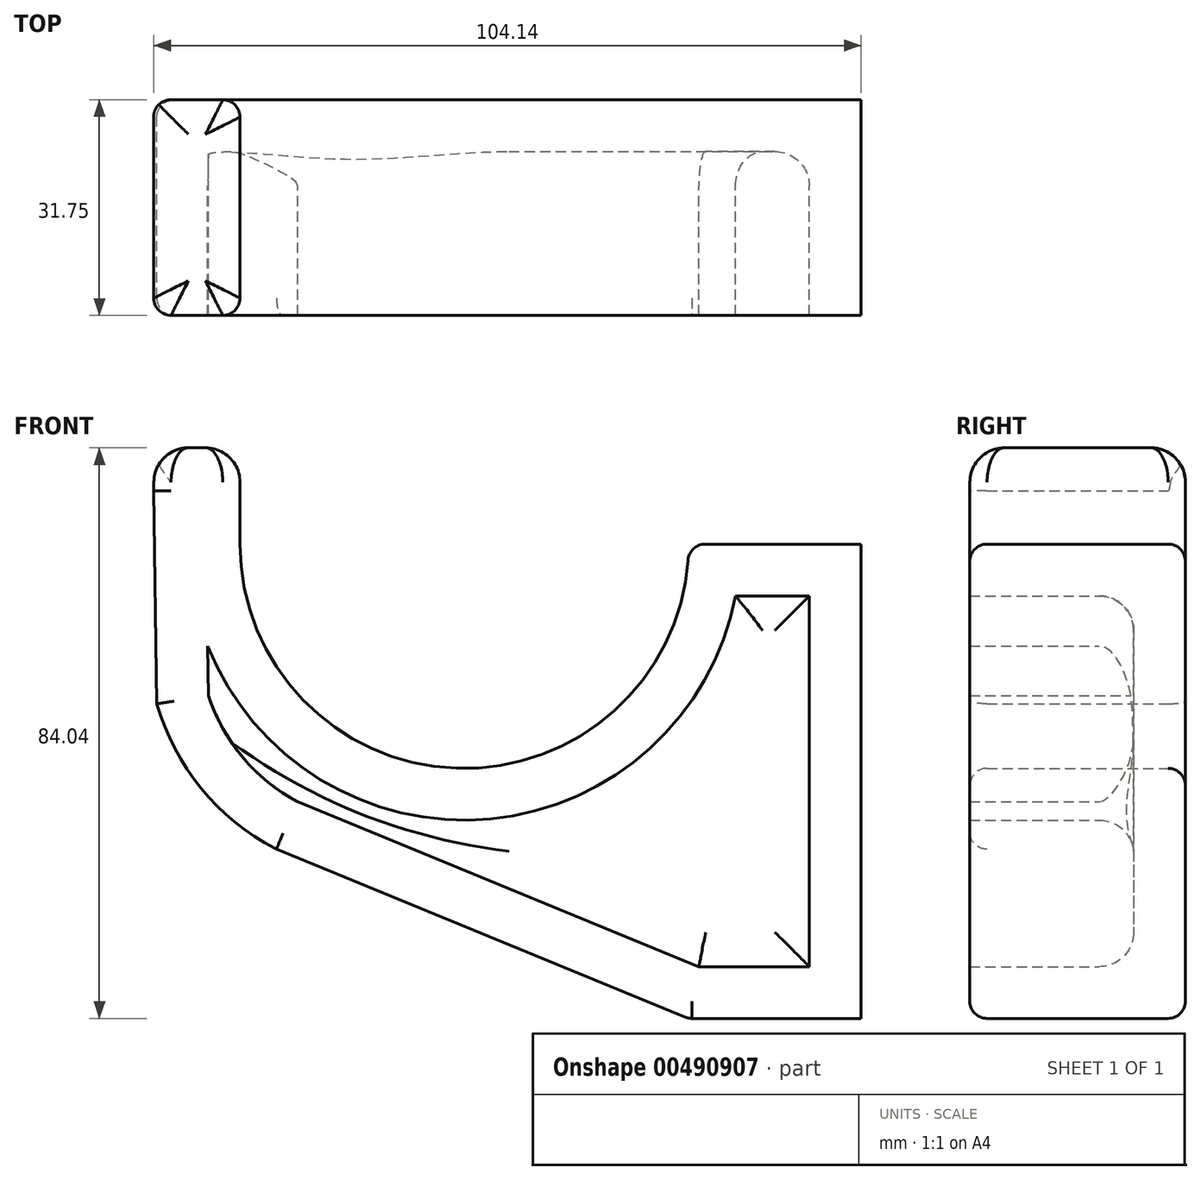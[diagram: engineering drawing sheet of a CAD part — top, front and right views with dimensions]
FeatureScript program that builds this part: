
annotation { "Feature Type Name" : "Feature", "Feature Type Description" : "" }
export const myFeature = defineFeature(function(context is Context, id is Id, definition is map)
    precondition{}
    {
        {
            var Q0;
            Q0=qCreatedBy(makeId("Front.planeOp"),FACE);
            var sketch = newSketch(context, id + "F0", { "sketchPlane" : qUnion([Q0])});
            skLineSegment(sketch, "E0", {"start": v(19.3, 23.5) * mm, "end": v(19.3, -46.34) * mm});
            skLineSegment(sketch, "E1", {"start": v(19.3, -46.34) * mm, "end": v(-6.1, -46.34) * mm});
            skLineSegment(sketch, "E2", {"start": v(-84.39, 0) * mm, "end": v(-84.84, 31.35) * mm});
            skArc(sketch, "E3", {"start": v(-72.14, 23.5) * mm, "mid": v(-39.12, -9.51) * mm, "end": v(-6.1, 23.5) * mm});
            skLineSegment(sketch, "E4", {"start": v(-6.1, 23.5) * mm, "end": v(19.3, 23.5) * mm});
            skLineSegment(sketch, "E5.top", {"start": v(-72.14, 37.7) * mm, "end": v(-84.84, 37.7) * mm});
            skLineSegment(sketch, "E5.left", {"start": v(-72.14, 23.5) * mm, "end": v(-72.14, 37.7) * mm});
            skLineSegment(sketch, "E5.right", {"start": v(-84.84, 17.4) * mm, "end": v(-84.84, 37.7) * mm});
            skArc(sketch, "E6", {"start": v(-84.39, 0) * mm, "mid": v(-77.83, -12.48) * mm, "end": v(-66.89, -21.36) * mm});
            skLineSegment(sketch, "E7", {"start": v(-66.89, -21.36) * mm, "end": v(-6.1, -46.34) * mm});
            skSolve(sketch);
        }
        {
            var Q0;
            Q0 = qSketchRegion(id + "F0", true);
            extrude(context, id + "F1", {"entities" : qUnion([Q0]), "depth" : 31.75 * mm});
        }
        {
            var Q0;
            Q0=makeQuery(id+"F1.opExtrude","CAP_FACE",FACE,{"disambiguationData":[OSD([sQuery(id+"F0.wireOp",EDGE,"E0"),sQuery(id+"F0.wireOp",EDGE,"E1"),sQuery(id+"F0.wireOp",EDGE,"E2"),sQuery(id+"F0.wireOp",EDGE,"E3"),sQuery(id+"F0.wireOp",EDGE,"E4"),sQuery(id+"F0.wireOp",EDGE,"E5.top"),sQuery(id+"F0.wireOp",EDGE,"E5.left"),sQuery(id+"F0.wireOp",EDGE,"E5.right"),sQuery(id+"F0.wireOp",EDGE,"E6"),sQuery(id+"F0.wireOp",EDGE,"E7")])],"isStart":false});
            shell(context, id + "F2", {"entities" : qUnion([Q0]), "thickness" : 7.62 * mm});
        }
        {
            var Q0;
            Q0=makeQuery(id+"F2.opShell","OFFSET_FACE",FACE,{"disambiguationData":[OSD([sQuery(id+"F0.wireOp",EDGE,"E0"),sQuery(id+"F0.wireOp",EDGE,"E1"),sQuery(id+"F0.wireOp",EDGE,"E2"),sQuery(id+"F0.wireOp",EDGE,"E3"),sQuery(id+"F0.wireOp",EDGE,"E4"),sQuery(id+"F0.wireOp",EDGE,"E5.top"),sQuery(id+"F0.wireOp",EDGE,"E5.left"),sQuery(id+"F0.wireOp",EDGE,"E5.right"),sQuery(id+"F0.wireOp",EDGE,"E6"),sQuery(id+"F0.wireOp",EDGE,"E7")])]});
            fillet(context, id + "F3", {"entities" : qUnion([Q0]), "radius" : 5.08 * mm, "tangentPropagation" : true, "allowEdgeOverflow" : false});
        }
        {
            var Q0;
            Q0=makeQuery(id+"F1.opExtrude","SWEPT_FACE",FACE,{"disambiguationData":[OSD([sQuery(id+"F0.wireOp",EDGE,"E5.top")])]});
            fillet(context, id + "F4", {"entities" : qUnion([Q0]), "radius" : 5.08 * mm, "tangentPropagation" : true, "allowEdgeOverflow" : false});
        }
        {
            var Q0;
            Q0=makeQuery(id+"F1.opExtrude","CAP_EDGE",EDGE,{"disambiguationData":[OSD([sQuery(id+"F0.wireOp",EDGE,"E4")])],"isStart":false});
            fillet(context, id + "F5", {"entities" : qUnion([Q0]), "radius" : 2.54 * mm, "tangentPropagation" : true, "allowEdgeOverflow" : false});
        }
        {
            var Q0;
            Q0=makeQuery(id+"F1.opExtrude","CAP_EDGE",EDGE,{"disambiguationData":[OSD([sQuery(id+"F0.wireOp",EDGE,"E4")])],"isStart":true});
            fillet(context, id + "F6", {"entities" : qUnion([Q0]), "radius" : 2.54 * mm, "tangentPropagation" : true, "allowEdgeOverflow" : false});
        }
        {
            var Q0;
            Q0=makeQuery(id+"F1.opExtrude","CAP_EDGE",EDGE,{"disambiguationData":[OSD([sQuery(id+"F0.wireOp",EDGE,"E1")])],"isStart":false});
            fillet(context, id + "F7", {"entities" : qUnion([Q0]), "radius" : 2.54 * mm, "tangentPropagation" : true, "allowEdgeOverflow" : false});
        }
        {
            var Q0;
            Q0=makeQuery(id+"F1.opExtrude","CAP_EDGE",EDGE,{"disambiguationData":[OSD([sQuery(id+"F0.wireOp",EDGE,"E7")])],"isStart":false});
            fillet(context, id + "F8", {"entities" : qUnion([Q0]), "radius" : 2.54 * mm, "tangentPropagation" : true, "allowEdgeOverflow" : false});
        }
        {
            var Q0;
            Q0=makeQuery(id+"F1.opExtrude","SWEPT_EDGE",EDGE,{"disambiguationData":[OSD([sQuery(id+"F0.wireOp",EDGE,"E3"),sQuery(id+"F0.wireOp",EDGE,"E4")])]});
            var Q1;
            Q1=makeQuery(id+"F1.opExtrude","CAP_EDGE",EDGE,{"disambiguationData":[OSD([sQuery(id+"F0.wireOp",EDGE,"E5.right")])],"isStart":false});
            var Q2;
            Q2=makeQuery(id+"F1.opExtrude","CAP_EDGE",EDGE,{"disambiguationData":[OSD([sQuery(id+"F0.wireOp",EDGE,"E2")])],"isStart":false});
            var Q3;
            Q3=makeQuery(id+"F1.opExtrude","CAP_EDGE",EDGE,{"disambiguationData":[OSD([sQuery(id+"F0.wireOp",EDGE,"E6")])],"isStart":false});
            fillet(context, id + "F9", {"entities" : qUnion([Q0, Q1, Q2, Q3]), "radius" : 2.54 * mm, "tangentPropagation" : true, "allowEdgeOverflow" : false});
        }
        {
            var Q0;
            Q0=makeQuery(id+"F1.opExtrude","CAP_EDGE",EDGE,{"disambiguationData":[OSD([sQuery(id+"F0.wireOp",EDGE,"E1")])],"isStart":true});
            var Q1;
            Q1=makeQuery(id+"F1.opExtrude","CAP_EDGE",EDGE,{"disambiguationData":[OSD([sQuery(id+"F0.wireOp",EDGE,"E7")])],"isStart":true});
            var Q2;
            Q2=makeQuery(id+"F1.opExtrude","CAP_EDGE",EDGE,{"disambiguationData":[OSD([sQuery(id+"F0.wireOp",EDGE,"E2")])],"isStart":true});
            fillet(context, id + "F10", {"entities" : qUnion([Q0, Q1, Q2]), "radius" : 2.54 * mm, "tangentPropagation" : true, "allowEdgeOverflow" : false});
        }
    });
